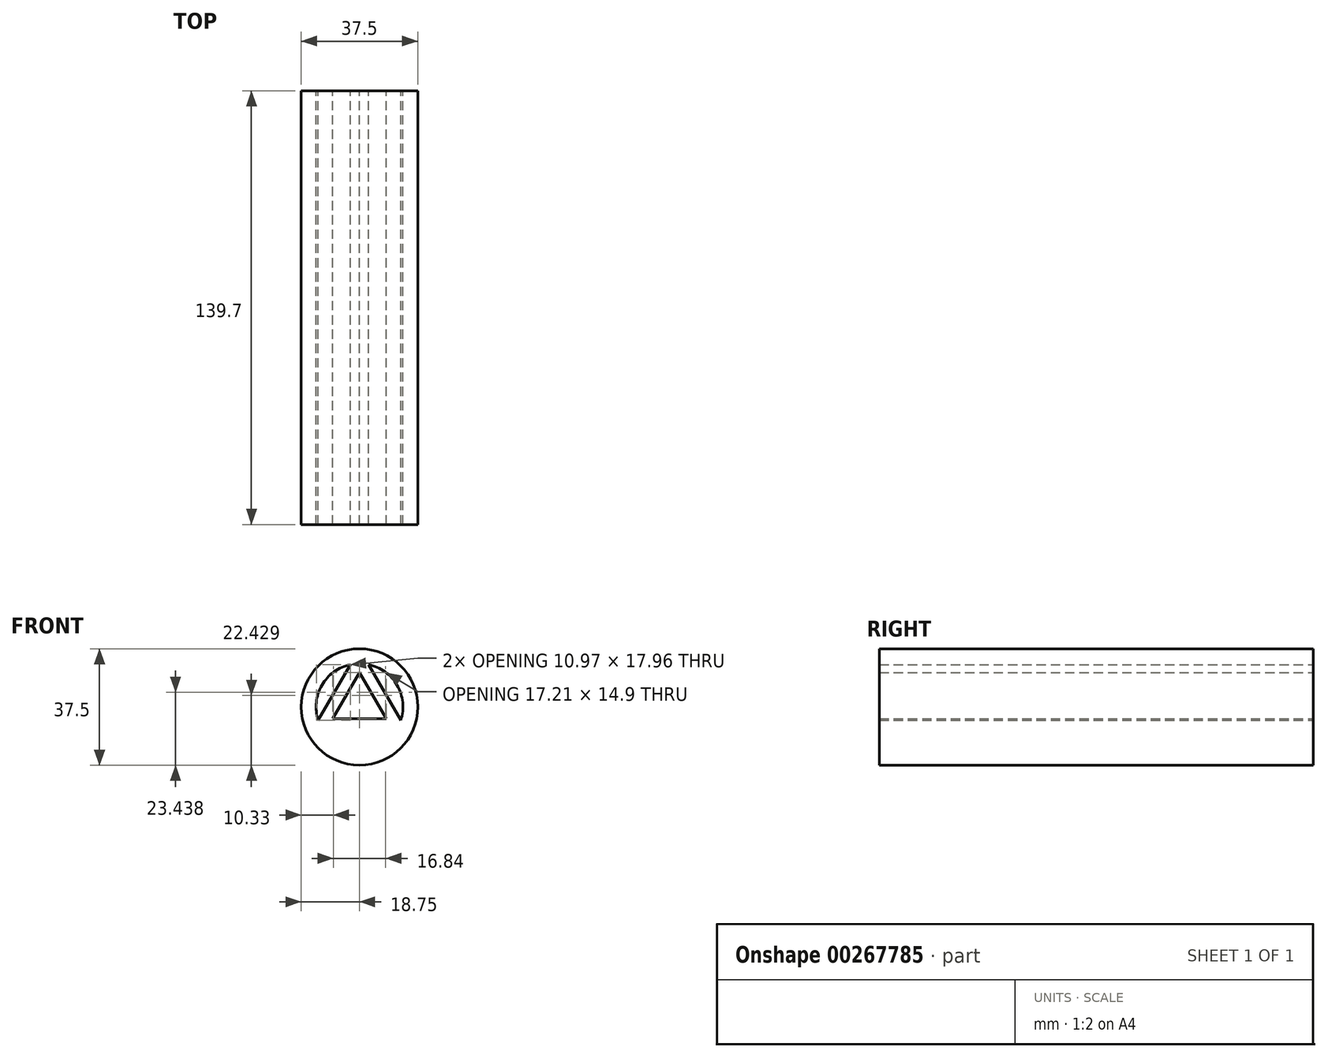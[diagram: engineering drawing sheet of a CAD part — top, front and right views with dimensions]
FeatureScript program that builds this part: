
annotation { "Feature Type Name" : "Feature", "Feature Type Description" : "" }
export const myFeature = defineFeature(function(context is Context, id is Id, definition is map)
    precondition{}
    {
        {
            var Q0;
            Q0=qCreatedBy(makeId("Front.planeOp"),FACE);
            var sketch = newSketch(context, id + "F0", { "sketchPlane" : qUnion([Q0])});
            skArc(sketch, "E0", {"start": v(-11.75, -7.58) * mm, "mid": v(0, -13.98) * mm, "end": v(11.75, -7.58) * mm});
            skCircle(sketch, "E1.0", {"center": v(0, 0) * mm, "radius": 18.75 * mm});
            skLineSegment(sketch, "E2", {"start": v(-2.93, 13.67) * mm, "end": v(-13.3, -4.3) * mm});
            skLineSegment(sketch, "E3", {"start": v(-11.75, -7.58) * mm, "end": v(11.75, -7.58) * mm});
            skLineSegment(sketch, "E4", {"start": v(13.3, -4.3) * mm, "end": v(2.93, 13.67) * mm});
            skPoint(sketch, "E5.orphan", {"position": v(0, 18.75) * mm});
            skLineSegment(sketch, "E6.0", {"start": v(0, 11.13) * mm, "end": v(-8.6, -3.77) * mm});
            skLineSegment(sketch, "E7.0", {"start": v(-8.6, -3.77) * mm, "end": v(8.6, -3.77) * mm});
            skLineSegment(sketch, "E8.0", {"start": v(8.6, -3.77) * mm, "end": v(0, 11.13) * mm});
            skArc(sketch, "E9.trimOffspring", {"start": v(13.3, -4.3) * mm, "mid": v(12.1, 7) * mm, "end": v(2.93, 13.67) * mm});
            skArc(sketch, "E10.trimOffspring", {"start": v(-2.93, 13.67) * mm, "mid": v(-12.1, 7) * mm, "end": v(-13.3, -4.3) * mm});
            skLineSegment(sketch, "E11.bottom", {"start": v(1.26, 16.3) * mm, "end": v(-1.55, 16.3) * mm});
            skLineSegment(sketch, "E11.top", {"start": v(1.26, 13.67) * mm, "end": v(-1.55, 13.67) * mm});
            skLineSegment(sketch, "E11.left", {"start": v(1.26, 16.3) * mm, "end": v(1.26, 13.67) * mm});
            skLineSegment(sketch, "E11.right", {"start": v(-1.55, 16.3) * mm, "end": v(-1.55, 13.67) * mm});
            skSolve(sketch);
        }
        {
            var Q0;
            Q0=makeQuery(id+"F0.imprint","IMPRINT",FACE,{"disambiguationData":[TD([[makeQuery(id+"F0.imprint","IMPRINT",EDGE,{"derivedFrom":sQuery(id+"F0.wireOp",EDGE,"ZBmzzGK3-CHHQ-1iO4-Gien-waH4lL1tLknt")}),1.0]])]});
            var Q1;
            Q1=makeQuery(id+"F0.imprint","IMPRINT",FACE,{"disambiguationData":[TD([[makeQuery(id+"F0.imprint","IMPRINT",EDGE,{"derivedFrom":sQuery(id+"F0.wireOp",EDGE,"E1.0")}),1.0]])]});
            var Q2;
            {var subQ0=sQuery(id+"F0.wireOp",EDGE,"E2");var subQ1=sQuery(id+"F0.wireOp",EDGE,"E0");var subQ2=makeQuery(id+"F0.imprint","INTERSECT",VERTEX,{"disambiguationData":[OD(0.0)],"derivedFrom":[subQ1,subQ0]});Q2=makeQuery(id+"F0.imprint","IMPRINT",FACE,{"disambiguationData":[TD([[makeQuery(id+"F0.imprint","IMPRINT",EDGE,{"disambiguationData":[TD([[subQ2,1.0]])],"derivedFrom":subQ1}),1.0]])]});}
            var Q3;
            Q3=makeQuery(id+"F0.imprint","IMPRINT",FACE,{"disambiguationData":[TD([[makeQuery(id+"F0.imprint","IMPRINT",EDGE,{"derivedFrom":sQuery(id+"F0.wireOp",EDGE,"E11.bottom")}),1.0]])]});
            extrude(context, id + "F1", {"entities" : qUnion([Q0, Q1, Q2, Q3]), "depth" : 139.7 * mm});
        }
    });
